# Revit family: ALPHI_ST
name_source: partatom
category: Equipement spécialisé
units: mm (PartAtom-declared; Revit-internal decimal feet)

## family parameters
Autoriser la découpe dans les vues = Non
Basée sur le plan de construction = Non
Conserver l'orientation des annotations = Non
Cote de connecteur circulaire = Utiliser le diamètre
Couper avec des vides une fois chargée = Non
Partagée = Non
Repère de localisation dans la pièce = Non
Toujours verticalement = Oui
Type d'élément = Normal

## types (1)
- ST1
    ALPHI_FOR_CHARGE UTILISATION = 32.00 kN
    ALPHI_FOR_V = 0.00 kN
    ALPHI_INE_I = 0.00 cm⁴
    ALPHI_LG_LARGEUR = 10 cm
    ALPHI_MAS_POIDS = 19.35 kg
    ALPHI_MAT_MATERIAU COULEUR TYPE = ALPHI_acier_laque_bleu
    ALPHI_MOM_M = 0.00 kN-m
    ALPHI_PRE_E = 0.0 MPa
    ALPHI_TXT_DESIGNATION = Support Technique ST1 (1,90 x 3,00 m)
    ALPHI_TXT_NOMENCLATURE_ABREVIATION = ST1
    ALPHI_TXT_NOMENCLATURE_DESIGNATION = Support technique N°1 (1,90 x 3,00 m)
    ALPHI_TXT_NOMENCLATURE_GAMME = Supports techniques
    ALPHI_VIS_VISIBILITE ST 1 = Oui
    ALPHI_VIS_VISIBILITE ST 2 = Non
    ALPHI_VIS_VISIBILITE ST 3 = Non
    Elévation par défaut = 0 cm
    LG_HAUTEUR ANNEAU = 146.5 cm
    LG_HAUTEUR COULISSE = 165.5 cm
    LG_HAUTEUR FUT = 131 cm
    LG_HAUTEUR MAXIMALE = 300 cm
    LG_HAUTEUR MINIMALE = 190 cm

## geometry (parser evidence)
native form markers: Blend x4
no freeform markers — native parametric forms only
